# Revit family: Palace_Multi_XO_Custom
name_source: partatom
category: Doors
revit_build: Autodesk Revit 2014 (Build: 20130308_1515(x64)
units: mm (PartAtom-declared; Revit-internal decimal feet)

## types (1)
- Palace-XO-Custom
    Area Left Sash Glazing = 1.17 m²
    Area Right Sash Glazing = 1.17 m²
    Centered In Wall = Yes
    Custom Door Height = 2090 mm  [stored 6.85696 ft]
    Custom Door Width = 1490 mm  [stored 4.88845 ft]
    Custom Frame Offset From Exterior = 0 mm  [stored 0 ft]
    Custom Sash Width Left = 600 mm  [stored 1.9685 ft]
    Custom Windload = 1000 mm  [stored 3.28084 ft]
    DG Air Gap Thickness = 12 mm  [stored 0.0393701 ft]
    DG Thickness Calc = 6 mm  [stored 0.019685 ft]
    Default Sill Height = 0 mm  [stored 0 ft]
    Description = High performance sliding door, XO custom
    Double Glazing Gasket Material = Double Glazing Gasket Material
    Equal Sash Width = Yes
    Frame Thickness = 118 mm
    Height = 2090 mm  [stored 6.85696 ft]
    Interlock Configuration = 0 mm  [stored 0 ft]
    Limit Door Height Max = 2390 mm  [stored 7.84121 ft]
    Limit Door Height Min = 359 mm  [stored 1.17782 ft]
    Limit Door Width Max = 2990 mm
    Limit Door Width Min = 626 mm
    Limit Sash Height Max = 2400 mm  [stored 7.87402 ft]
    Limit Sash Height Min = 300 mm  [stored 0.984252 ft]
    Limit Sash Width Left Max = 1164 mm  [stored 3.8189 ft]
    Limit Sash Width Left Min = 300 mm  [stored 0.984252 ft]
    Limit Sash Width Max = 1500 mm  [stored 4.92126 ft]
    Limit Sash Width Min = 300 mm  [stored 0.984252 ft]
    Manufacturer = Crealco
    Max Pane Area = 1.17 m²
    Max System DG One Piece Thickness = 6 mm  [stored 0.019685 ft]
    Max System DG Unit Thickness = 25 mm  [stored 0.082021 ft]
    Model = Palace
    Rough Width = 3 mm  [stored 0.00984252 ft]
    Sash Bottom Gap = 31 mm  [stored 0.101706 ft]
    Sash Frame Seal = 3 mm  [stored 0.00984252 ft]
    Sash Height = 2031 mm  [stored 6.66339 ft]
    Sash Interlocker Width = 40 mm  [stored 0.131234 ft]
    Sash Side Gap = 33 mm  [stored 0.108268 ft]
    Sash Top Gap = 28 mm  [stored 0.0918635 ft]
    Sash Width Left = 732 mm  [stored 2.40157 ft]
    Sash Width Right = 732 mm  [stored 2.40157 ft]
    Thickness = 758 mm
    URL = http://www.crealco.co.za
    Wall Closure = By host
    Width = 1490 mm  [stored 4.88845 ft]
    Windload Design = 1000 mm  [stored 3.28084 ft]

note: [stored X ft] marks values corroborated as IEEE doubles in the binary element streams (Revit-internal decimal feet)

## geometry (parser evidence)
native form markers: Sweep x51
no freeform markers — native parametric forms only
